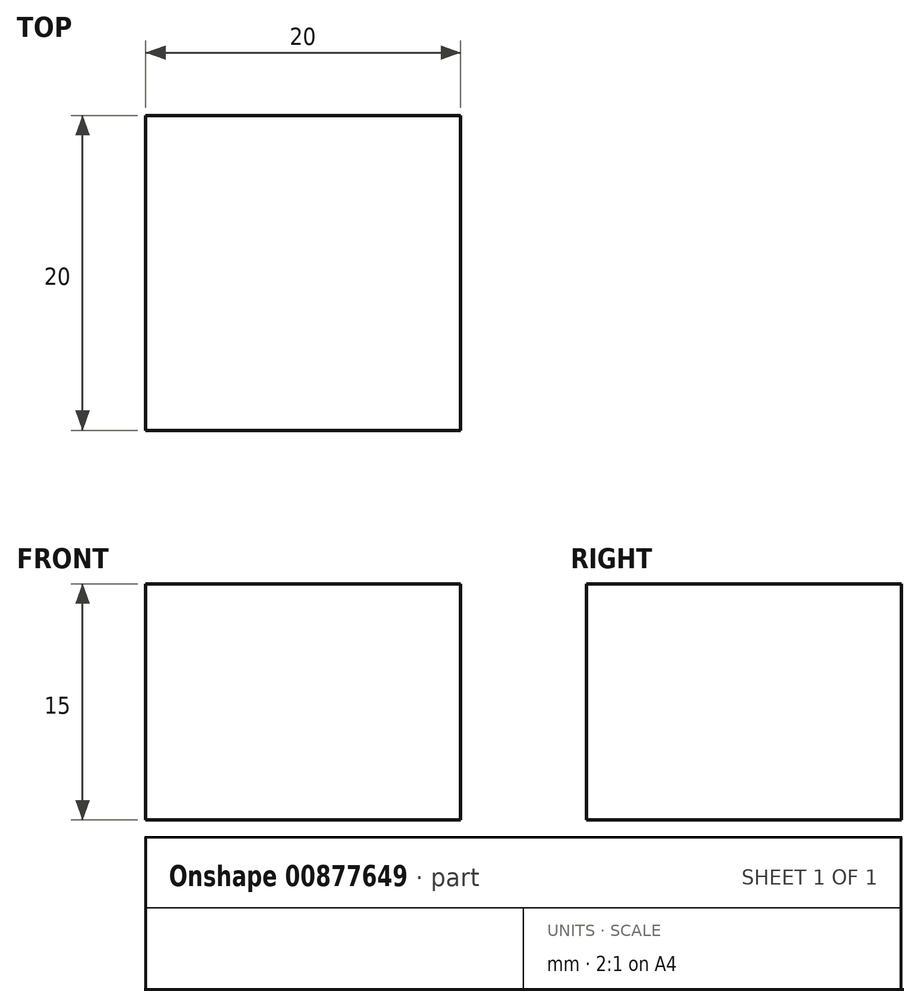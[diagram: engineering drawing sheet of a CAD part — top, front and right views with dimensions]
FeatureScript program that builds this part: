
annotation { "Feature Type Name" : "Feature", "Feature Type Description" : "" }
export const myFeature = defineFeature(function(context is Context, id is Id, definition is map)
    precondition{}
    {
        {
            var Q0;
            Q0=qCreatedBy(makeId("Top.planeOp"),FACE);
            var sketch = newSketch(context, id + "F0", { "sketchPlane" : qUnion([Q0])});
            skLineSegment(sketch, "E0.bottom", {"start": v(0, 0) * mm, "end": v(20, 0) * mm});
            skLineSegment(sketch, "E0.top", {"start": v(0, -20) * mm, "end": v(20, -20) * mm});
            skLineSegment(sketch, "E0.left", {"start": v(0, 0) * mm, "end": v(0, -20) * mm});
            skLineSegment(sketch, "E0.right", {"start": v(20, 0) * mm, "end": v(20, -20) * mm});
            skSolve(sketch);
        }
        {
            var Q0;
            Q0=makeQuery(id+"F0.imprint","IMPRINT",FACE,{"disambiguationData":[TD([[makeQuery(id+"F0.imprint","IMPRINT",EDGE,{"derivedFrom":sQuery(id+"F0.wireOp",EDGE,"E0.bottom")}),-1.0]])]});
            extrude(context, id + "F1", {"entities" : qUnion([Q0]), "depth" : 15 * mm, "offsetDistance" : 25 * mm});
        }
    });
